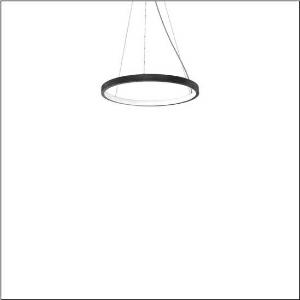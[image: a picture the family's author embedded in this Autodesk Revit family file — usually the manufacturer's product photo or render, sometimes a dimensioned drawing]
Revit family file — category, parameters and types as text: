
# Revit family: silica_21_ring-i_5pjbi1d3104a
name_source: partatom
category: Lighting Fixtures
units: mm (PartAtom-declared; Revit-internal decimal feet)

## family parameters
Cut with Voids When Loaded = No
Host = Face
Light Source = No
Part Type = Normal
Room Calculation Point = No
Round Connector Dimension = Use Diameter
Shared = No

## types (1)
- Silica 21 Ring-I (1 x LED, 3510 lm, 60 W, 4000K)
    Apparent Load = 60 VA
    CIE Flux Codes = 22 48 76 50 101
    Color Rendering = 80
    Color Temperature = 4000K
    Default Elevation = 1800 mm
    Description = Silica 21 Ring-I, suspended luminaire, of PMMA, frosted, light emission: inner ring side luminous distribution, primary light characteristic: symmetric, installation type: suspended mounting, LED, rated luminous flux: 3.510lm, luminous efficacy: 59lm/W, light colour: 840, colour temperature: 4000K, control gear: DALI 2, with terminal, 5-pole, mains connection: 230V, AC/DC, 0/50..60Hz, rated input power: 60W, housing, of extruded aluminium section, jet black (RAL 9005), diameter: 610mm, ceiling canopy, jet black (RAL 9005), protection rating (lamp compartment): IP40, insulation class (complete): insulation class I (protective earthing), certification: CE, impact resistance: IK02, permissible operating ambient temperature: 0..+35°C, packaging unit: 1 piece
    Height = 48 mm  [stored 0.15748 ft]
    Lamp = 1 x LED
    Lamp Light Flux = 3510 lm
    Lamp Power = 60 W
    Lamp count = 1
    Length = 610 mm
    Luminous efficacy = 59 lm/W
    Manufacturer = Siteco
    ModVariant = No
    Model = 5PJBI1D3104A
    Mounting Place = Ceiling
    Mounting Type = Pendant
    Number of Poles = 1
    OnlyDefault = Yes
    Power Factor = 1
    Product Name = Silica 21 Ring-I
    Product group = suspended luminaire
    ProductGroupID = 904
    Protection Class = Protection class I
    Protection Degree = IP 40
    RLX_Detail_Level = 1
    RLX_Emergency_Light_Flux = 0 lm
    RLX_Emergency_Type = 0
    RLX_Emergency_Type_DB = No
    RlxData = <blob elided: 12353 chars, md5=29ee7121>
    Socket = socket
    Standby Power = 0 W
    System Light Flux = 3510 lm
    System Power = 60 W
    Type Comments = Product without accessories
    Type Image = l_1258361.jpg
    URL = http://relux.com
    VarID = ---
    Voltage = 0 V
    Weight = 0.00 kg
    Width = 0 mm  [stored 0 ft]

note: [stored X ft] marks values corroborated as IEEE doubles in the binary element streams (Revit-internal decimal feet)

## geometry (parser evidence)
native form markers: Sweep x12
no freeform markers — native parametric forms only
